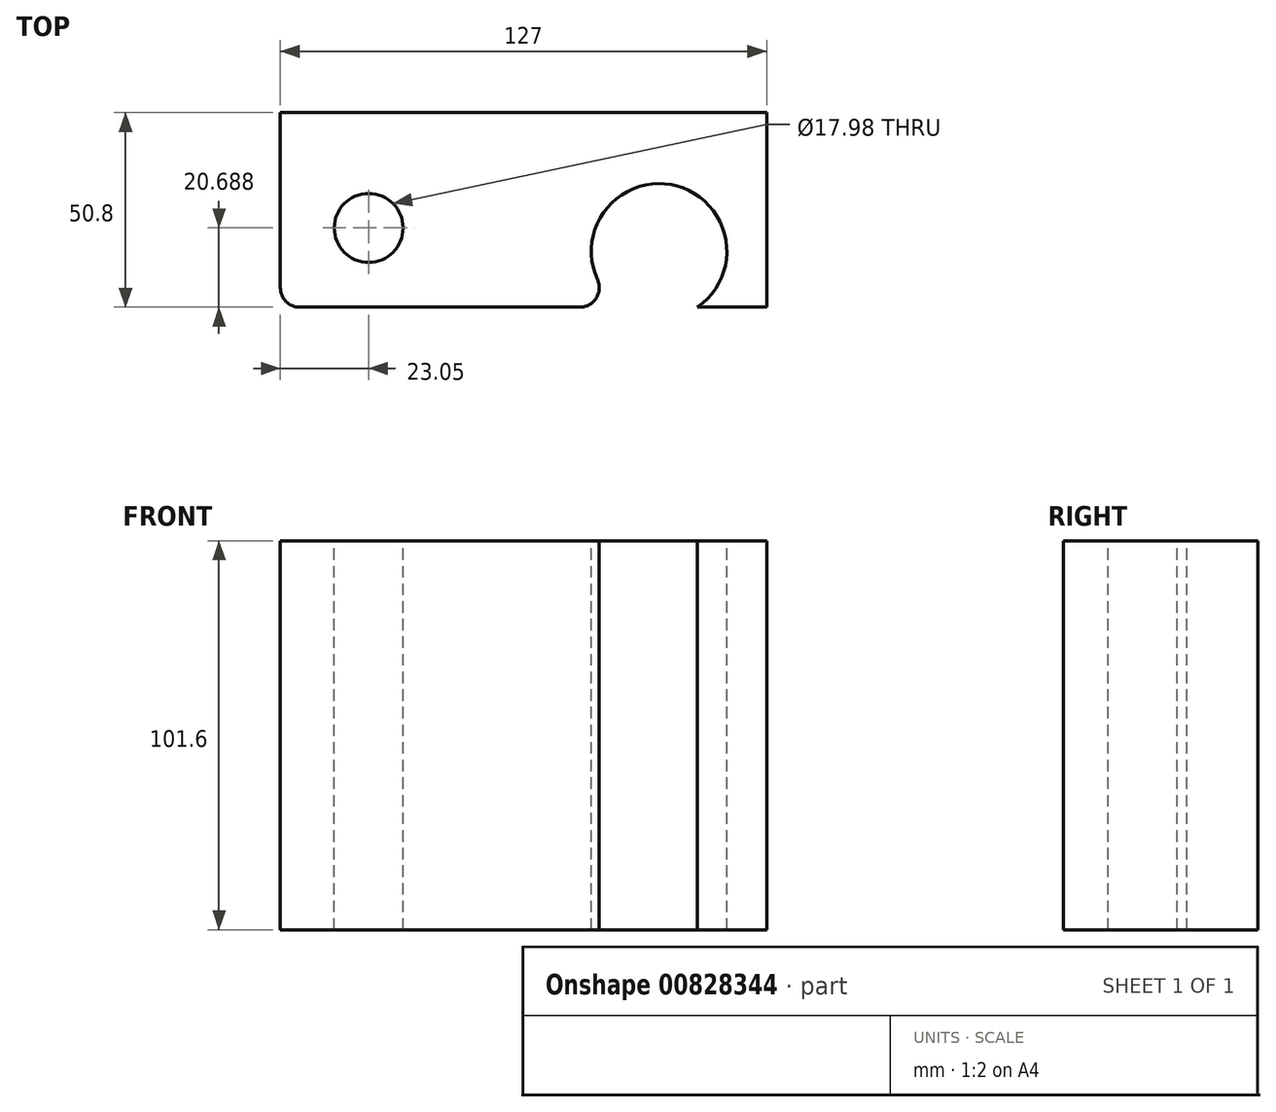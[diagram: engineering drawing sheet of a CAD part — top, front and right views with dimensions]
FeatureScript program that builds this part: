
annotation { "Feature Type Name" : "Feature", "Feature Type Description" : "" }
export const myFeature = defineFeature(function(context is Context, id is Id, definition is map)
    precondition{}
    {
        {
            var Q0;
            Q0=qCreatedBy(makeId("Front.planeOp"),FACE);
            var sketch = newSketch(context, id + "F0", { "sketchPlane" : qUnion([Q0])});
            skLineSegment(sketch, "E0.bottom", {"start": v(63.5, 50.8) * mm, "end": v(-63.5, 50.8) * mm});
            skLineSegment(sketch, "E0.top", {"start": v(63.5, -50.8) * mm, "end": v(-63.5, -50.8) * mm});
            skLineSegment(sketch, "E0.left", {"start": v(63.5, 50.8) * mm, "end": v(63.5, -50.8) * mm});
            skLineSegment(sketch, "E0.right", {"start": v(-63.5, 50.8) * mm, "end": v(-63.5, -50.8) * mm});
            skPoint(sketch, "E0.middle", {"position": v(0, 0) * mm});
            skSolve(sketch);
        }
        {
            var Q0;
            Q0 = qSketchRegion(id + "F0", true);
            extrude(context, id + "F1", {"entities" : qUnion([Q0]), "endBound" : BoundingType.SYMMETRIC, "depth" : 50.8 * mm, "offsetDistance" : 25.4 * mm});
        }
        {
            var Q0;
            Q0=makeQuery(id+"F1.opExtrude","SWEPT_FACE",FACE,{"disambiguationData":[OSD([sQuery(id+"F0.wireOp",EDGE,"E0.bottom")])]});
            var sketch = newSketch(context, id + "F2", { "sketchPlane" : qUnion([Q0])});
            skCircle(sketch, "E1", {"center": v(-40.45, -4.71) * mm, "radius": 8.99 * mm});
            skCircle(sketch, "E2", {"center": v(35.41, -10.83) * mm, "radius": 17.7 * mm});
            skSolve(sketch);
        }
        {
            var Q0;
            Q0=makeQuery(id+"F2.imprint","IMPRINT",FACE,{"disambiguationData":[TD([[makeQuery(id+"F2.imprint","IMPRINT",EDGE,{"derivedFrom":sQuery(id+"F2.wireOp",EDGE,"E1")}),1.0]])]});
            var Q1;
            {var subQ0=sQuery(id+"F2.wireOp",EDGE,"E2");var subQ1=makeQuery(id+"F1.opExtrude","CAP_EDGE",EDGE,{"disambiguationData":[OSD([sQuery(id+"F0.wireOp",EDGE,"E0.bottom")])],"isStart":false});var subQ2=makeQuery(id+"F2.imprint","INTERSECT",VERTEX,{"disambiguationData":[OD(0.0)],"derivedFrom":[subQ1,subQ0]});Q1=makeQuery(id+"F2.imprint","IMPRINT",FACE,{"disambiguationData":[TD([[makeQuery(id+"F2.imprint","IMPRINT",EDGE,{"disambiguationData":[TD([[subQ2,-1.0]])],"derivedFrom":subQ0}),1.0]])]});}
            extrude(context, id + "F3", {"entities" : qUnion([Q0, Q1]), "operationType" : NewBodyOperationType.REMOVE, "endBound" : BoundingType.UP_TO_NEXT, "oppositeDirection" : true, "depth" : 25.4 * mm, "offsetDistance" : 25.4 * mm});
        }
        {
            var Q0;
            {var subQ0=sQuery(id+"F2.wireOp",EDGE,"E2");var subQ1=sQuery(id+"F0.wireOp",EDGE,"E0.bottom");Q0=makeQuery(id+"F3.boolean.opBoolean","COPY",EDGE,{"derivedFrom":makeQuery(id+"F3.opExtrude","SWEPT_EDGE",EDGE,{"disambiguationData":[OSD([subQ1,subQ0]),TDD([makeQuery(id+"F2.imprint","INTERSECT",VERTEX,{"disambiguationData":[OD(1.0)],"derivedFrom":[makeQuery(id+"F1.opExtrude","CAP_EDGE",EDGE,{"disambiguationData":[OSD([subQ1])],"isStart":false}),subQ0]})])]})});}
            var Q1;
            {var subQ0=sQuery(id+"F2.wireOp",EDGE,"E2");var subQ1=sQuery(id+"F0.wireOp",EDGE,"E0.bottom");Q1=makeQuery(id+"F3.boolean.opBoolean","COPY",EDGE,{"derivedFrom":makeQuery(id+"F3.opExtrude","SWEPT_EDGE",EDGE,{"disambiguationData":[OSD([subQ1,subQ0]),TDD([makeQuery(id+"F2.imprint","INTERSECT",VERTEX,{"disambiguationData":[OD(0.0)],"derivedFrom":[makeQuery(id+"F1.opExtrude","CAP_EDGE",EDGE,{"disambiguationData":[OSD([subQ1])],"isStart":false}),subQ0]})])]})});}
            var Q2;
            Q2=makeQuery(id+"F1.opExtrude","CAP_EDGE",EDGE,{"disambiguationData":[OSD([sQuery(id+"F0.wireOp",EDGE,"E0.right")])],"isStart":false});
            var Q3;
            Q3=makeQuery(id+"F3.boolean.opBoolean","COPY",EDGE,{"derivedFrom":makeQuery(id+"F3.opExtrude","CAP_EDGE",EDGE,{"disambiguationData":[OSD([sQuery(id+"F2.wireOp",EDGE,"E1")])],"isStart":true})});
            var Q4;
            Q4=makeQuery(id+"F3.boolean.opBoolean","COPY",EDGE,{"derivedFrom":makeQuery(id+"F3.opExtrude","CAP_EDGE",EDGE,{"disambiguationData":[OSD([sQuery(id+"F2.wireOp",EDGE,"E2")])],"isStart":true})});
            var Q5;
            Q5=makeQuery(id+"F3.boolean.opBoolean","COPY",EDGE,{"derivedFrom":makeQuery(id+"F3.opExtrude","CAP_EDGE",EDGE,{"disambiguationData":[OSD([sQuery(id+"F2.wireOp",EDGE,"E2")])],"isStart":false})});
            fillet(context, id + "F4", {"entities" : qUnion([Q0, Q1, Q2, Q3, Q4, Q5]), "radius" : 5.08 * mm, "tangentPropagation" : true, "allowEdgeOverflow" : false});
        }
    });
